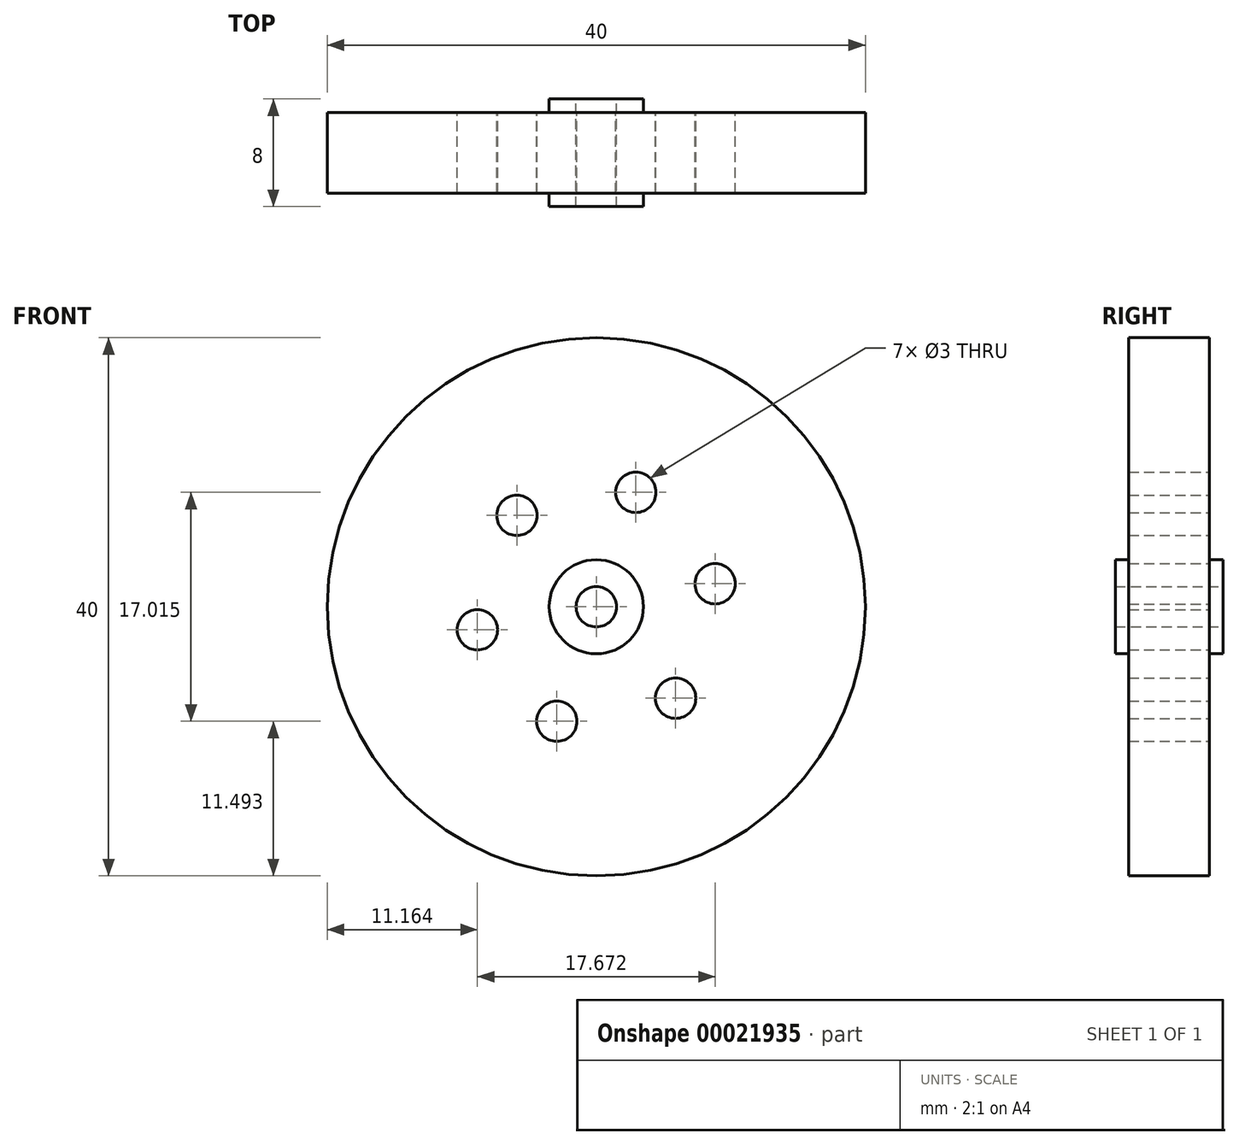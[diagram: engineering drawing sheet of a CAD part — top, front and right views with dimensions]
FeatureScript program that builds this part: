
annotation { "Feature Type Name" : "Feature", "Feature Type Description" : "" }
export const myFeature = defineFeature(function(context is Context, id is Id, definition is map)
    precondition{}
    {
        {
            var Q0;
            Q0=qCreatedBy(makeId("Front.planeOp"),FACE);
            var sketch = newSketch(context, id + "F0", { "sketchPlane" : qUnion([Q0])});
            skCircle(sketch, "E0", {"center": v(0, 0) * mm, "radius": 20 * mm});
            skCircle(sketch, "E1", {"center": v(0, 0) * mm, "radius": 3.5 * mm});
            skCircle(sketch, "E2", {"center": v(0, 0) * mm, "radius": 1.5 * mm});
            skCircle(sketch, "E3", {"center": v(-5.9, 6.8) * mm, "radius": 1.5 * mm});
            skCircle(sketch, "E4.1.0", {"center": v(-8.84, -1.71) * mm, "radius": 1.5 * mm});
            skCircle(sketch, "E4.2.0", {"center": v(-2.94, -8.5) * mm, "radius": 1.5 * mm});
            skCircle(sketch, "E4.3.0", {"center": v(5.9, -6.8) * mm, "radius": 1.5 * mm});
            skCircle(sketch, "E4.4.0", {"center": v(8.84, 1.71) * mm, "radius": 1.5 * mm});
            skCircle(sketch, "E4.5.0", {"center": v(2.94, 8.5) * mm, "radius": 1.5 * mm});
            skSolve(sketch);
        }
        {
            var Q0;
            Q0=makeQuery(id+"F0.imprint","IMPRINT",FACE,{"disambiguationData":[TD([[makeQuery(id+"F0.imprint","IMPRINT",EDGE,{"derivedFrom":sQuery(id+"F0.wireOp",EDGE,"E0")}),1.0]])]});
            extrude(context, id + "F1", {"entities" : qUnion([Q0]), "endBound" : BoundingType.SYMMETRIC, "depth" : 6 * mm});
        }
        {
            var Q0;
            Q0=makeQuery(id+"F0.imprint","IMPRINT",FACE,{"disambiguationData":[TD([[makeQuery(id+"F0.imprint","IMPRINT",EDGE,{"derivedFrom":sQuery(id+"F0.wireOp",EDGE,"E1")}),1.0]])]});
            extrude(context, id + "F2", {"entities" : qUnion([Q0]), "operationType" : NewBodyOperationType.ADD, "endBound" : BoundingType.SYMMETRIC, "depth" : 8 * mm});
        }
    });
